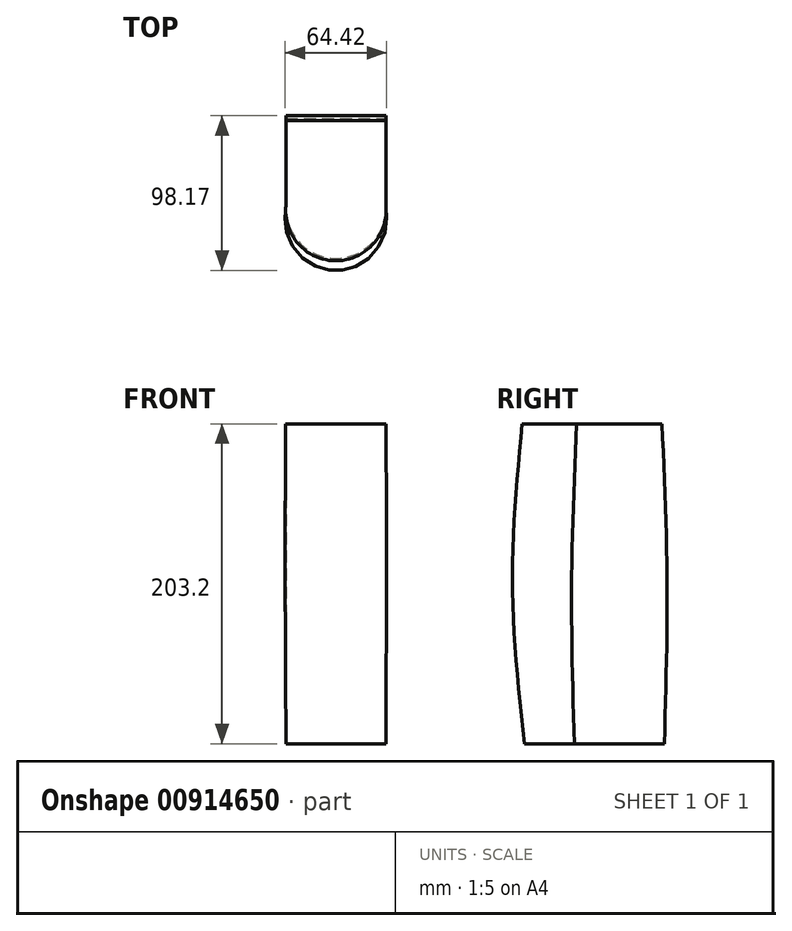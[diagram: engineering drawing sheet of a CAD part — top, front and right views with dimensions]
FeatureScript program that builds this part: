
annotation { "Feature Type Name" : "Feature", "Feature Type Description" : "" }
export const myFeature = defineFeature(function(context is Context, id is Id, definition is map)
    precondition{}
    {
        {
            var Q0;
            Q0=qCreatedBy(makeId("Top.planeOp"),FACE);
            var sketch = newSketch(context, id + "F0", { "sketchPlane" : qUnion([Q0])});
            skLineSegment(sketch, "E0.bottom", {"start": v(-31.75, 28.57) * mm, "end": v(31.75, 28.57) * mm});
            skLineSegment(sketch, "E0.left", {"start": v(-31.75, 28.57) * mm, "end": v(-31.75, -28.57) * mm});
            skLineSegment(sketch, "E0.right", {"start": v(31.75, 28.57) * mm, "end": v(31.75, -28.57) * mm});
            skPoint(sketch, "E0.middle", {"position": v(0, 0) * mm});
            skArc(sketch, "E1", {"start": v(-31.75, -28.57) * mm, "mid": v(0, -60.33) * mm, "end": v(31.75, -28.57) * mm});
            skSolve(sketch);
        }
        {
            var Q0;
            Q0=qCreatedBy(makeId("Top.planeOp"),FACE);
            cPlane(context, id + "F1", {"entities" : qUnion([Q0]), "cplaneType" : CPlaneType.OFFSET, "offset" : 101.6 * mm, "width" : 152.4 * mm, "height" : 152.4 * mm});
        }
        {
            var Q0;
            Q0=qCreatedBy(id+"F1.planeOp",FACE);
            var sketch = newSketch(context, id + "F2", { "sketchPlane" : qUnion([Q0])});
            skLineSegment(sketch, "E2.left", {"start": v(31.75, -30.3) * mm, "end": v(31.75, 30.3) * mm});
            skLineSegment(sketch, "E2.right", {"start": v(-31.75, -30.3) * mm, "end": v(-31.75, 30.3) * mm});
            skPoint(sketch, "E2.middle", {"position": v(0, 0) * mm});
            skLineSegment(sketch, "E3", {"start": v(31.75, 30.3) * mm, "end": v(-31.75, 30.3) * mm});
            skArc(sketch, "E4", {"start": v(-31.75, -30.3) * mm, "mid": v(0, -67.83) * mm, "end": v(31.75, -30.3) * mm});
            skSolve(sketch);
        }
        {
            var Q0;
            Q0=qCreatedBy(id+"F1.planeOp",FACE);
            cPlane(context, id + "F3", {"entities" : qUnion([Q0]), "cplaneType" : CPlaneType.OFFSET, "offset" : 101.6 * mm, "width" : 152.4 * mm, "height" : 152.4 * mm});
        }
        {
            var Q0;
            Q0=qCreatedBy(id+"F3.planeOp",FACE);
            var sketch = newSketch(context, id + "F4", { "sketchPlane" : qUnion([Q0])});
            skLineSegment(sketch, "E5.bottom", {"start": v(-31.76, 27.13) * mm, "end": v(31.75, 27.13) * mm});
            skLineSegment(sketch, "E5.left", {"start": v(-31.76, 27.13) * mm, "end": v(-31.76, -27.13) * mm});
            skLineSegment(sketch, "E5.right", {"start": v(31.75, 27.13) * mm, "end": v(31.75, -27.13) * mm});
            skPoint(sketch, "E5.middle", {"position": v(0, 0) * mm});
            skArc(sketch, "E6", {"start": v(-31.76, -27.13) * mm, "mid": v(0, -61.77) * mm, "end": v(31.75, -27.13) * mm});
            skSolve(sketch);
        }
        {
            var Q0;
            Q0=makeQuery(id+"F4.imprint","IMPRINT",FACE,{"disambiguationData":[TD([[makeQuery(id+"F4.imprint","IMPRINT",EDGE,{"derivedFrom":sQuery(id+"F4.wireOp",EDGE,"E5.bottom")}),-1.0]])]});
            var Q1;
            Q1=makeQuery(id+"F2.imprint","IMPRINT",FACE,{"disambiguationData":[TD([[makeQuery(id+"F2.imprint","IMPRINT",EDGE,{"derivedFrom":sQuery(id+"F2.wireOp",EDGE,"E2.left")}),1.0]])]});
            var Q2;
            Q2=makeQuery(id+"F0.imprint","IMPRINT",FACE,{"disambiguationData":[TD([[makeQuery(id+"F0.imprint","IMPRINT",EDGE,{"derivedFrom":sQuery(id+"F0.wireOp",EDGE,"E0.bottom")}),-1.0]])]});
            loft(context, id + "F5", {"sheetProfilesArray" : [{ "sheetProfileEntities" : qUnion([Q0]) }, { "sheetProfileEntities" : qUnion([Q1]) }, { "sheetProfileEntities" : qUnion([Q2]) }]});
        }
    });
